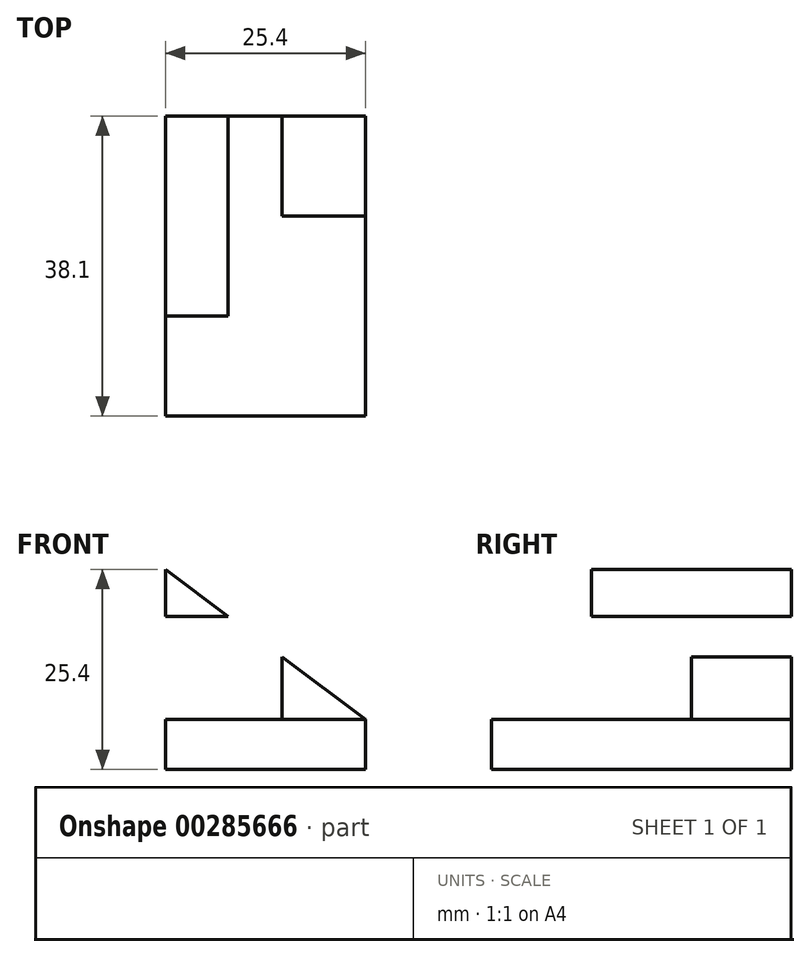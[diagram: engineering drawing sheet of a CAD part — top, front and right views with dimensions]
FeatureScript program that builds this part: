
annotation { "Feature Type Name" : "Feature", "Feature Type Description" : "" }
export const myFeature = defineFeature(function(context is Context, id is Id, definition is map)
    precondition{}
    {
        {
            var Q0;
            Q0=qCreatedBy(makeId("Front.planeOp"),FACE);
            var sketch = newSketch(context, id + "F0", { "sketchPlane" : qUnion([Q0])});
            skLineSegment(sketch, "E0", {"start": v(0, 0) * mm, "end": v(0, 25.4) * mm});
            skLineSegment(sketch, "E1", {"start": v(0, 0) * mm, "end": v(25.4, 0) * mm});
            skLineSegment(sketch, "E2", {"start": v(25.4, 0) * mm, "end": v(25.4, 6.35) * mm});
            skLineSegment(sketch, "E3", {"start": v(25.4, 6.35) * mm, "end": v(0, 25.4) * mm});
            skLineSegment(sketch, "E4", {"start": v(25.4, 6.35) * mm, "end": v(0, 6.35) * mm});
            skLineSegment(sketch, "E5", {"start": v(0, 6.35) * mm, "end": v(0, 0) * mm});
            skLineSegment(sketch, "E6", {"start": v(0, 19.45) * mm, "end": v(7.94, 19.45) * mm});
            skLineSegment(sketch, "E7", {"start": v(7.94, 19.45) * mm, "end": v(0, 25.4) * mm});
            skLineSegment(sketch, "E8", {"start": v(0, 25.4) * mm, "end": v(0, 19.45) * mm});
            skLineSegment(sketch, "E9", {"start": v(14.82, 14.29) * mm, "end": v(14.82, 6.35) * mm});
            skLineSegment(sketch, "E10", {"start": v(14.82, 6.35) * mm, "end": v(25.4, 6.35) * mm});
            skLineSegment(sketch, "E11", {"start": v(25.4, 6.35) * mm, "end": v(14.82, 14.29) * mm});
            skSolve(sketch);
        }
        {
            var Q0;
            Q0=makeQuery(id+"F0.imprint","IMPRINT",FACE,{"disambiguationData":[TD([[makeQuery(id+"F0.imprint","IMPRINT",EDGE,{"derivedFrom":sQuery(id+"F0.wireOp",EDGE,"E1")}),1.0]])]});
            extrude(context, id + "F1", {"entities" : qUnion([Q0]), "depth" : 38.1 * mm});
        }
        {
            var Q0;
            Q0=makeQuery(id+"F0.imprint","IMPRINT",FACE,{"disambiguationData":[TD([[makeQuery(id+"F0.imprint","IMPRINT",EDGE,{"derivedFrom":sQuery(id+"F0.wireOp",EDGE,"E0")}),-1.0]])]});
            extrude(context, id + "F2", {"entities" : qUnion([Q0]), "operationType" : NewBodyOperationType.ADD, "depth" : 25.4 * mm});
        }
        {
            var Q0;
            Q0=makeQuery(id+"F0.imprint","IMPRINT",FACE,{"disambiguationData":[TD([[makeQuery(id+"F0.imprint","IMPRINT",EDGE,{"derivedFrom":sQuery(id+"F0.wireOp",EDGE,"E6")}),1.0]])]});
            extrude(context, id + "F3", {"entities" : qUnion([Q0]), "operationType" : NewBodyOperationType.ADD, "depth" : 12.7 * mm});
        }
        {
            var Q0;
            Q0=makeQuery(id+"F0.imprint","IMPRINT",FACE,{"disambiguationData":[TD([[makeQuery(id+"F0.imprint","IMPRINT",EDGE,{"derivedFrom":sQuery(id+"F0.wireOp",EDGE,"E9")}),1.0]])]});
            extrude(context, id + "F4", {"entities" : qUnion([Q0]), "operationType" : NewBodyOperationType.ADD, "depth" : 12.7 * mm});
        }
    });
